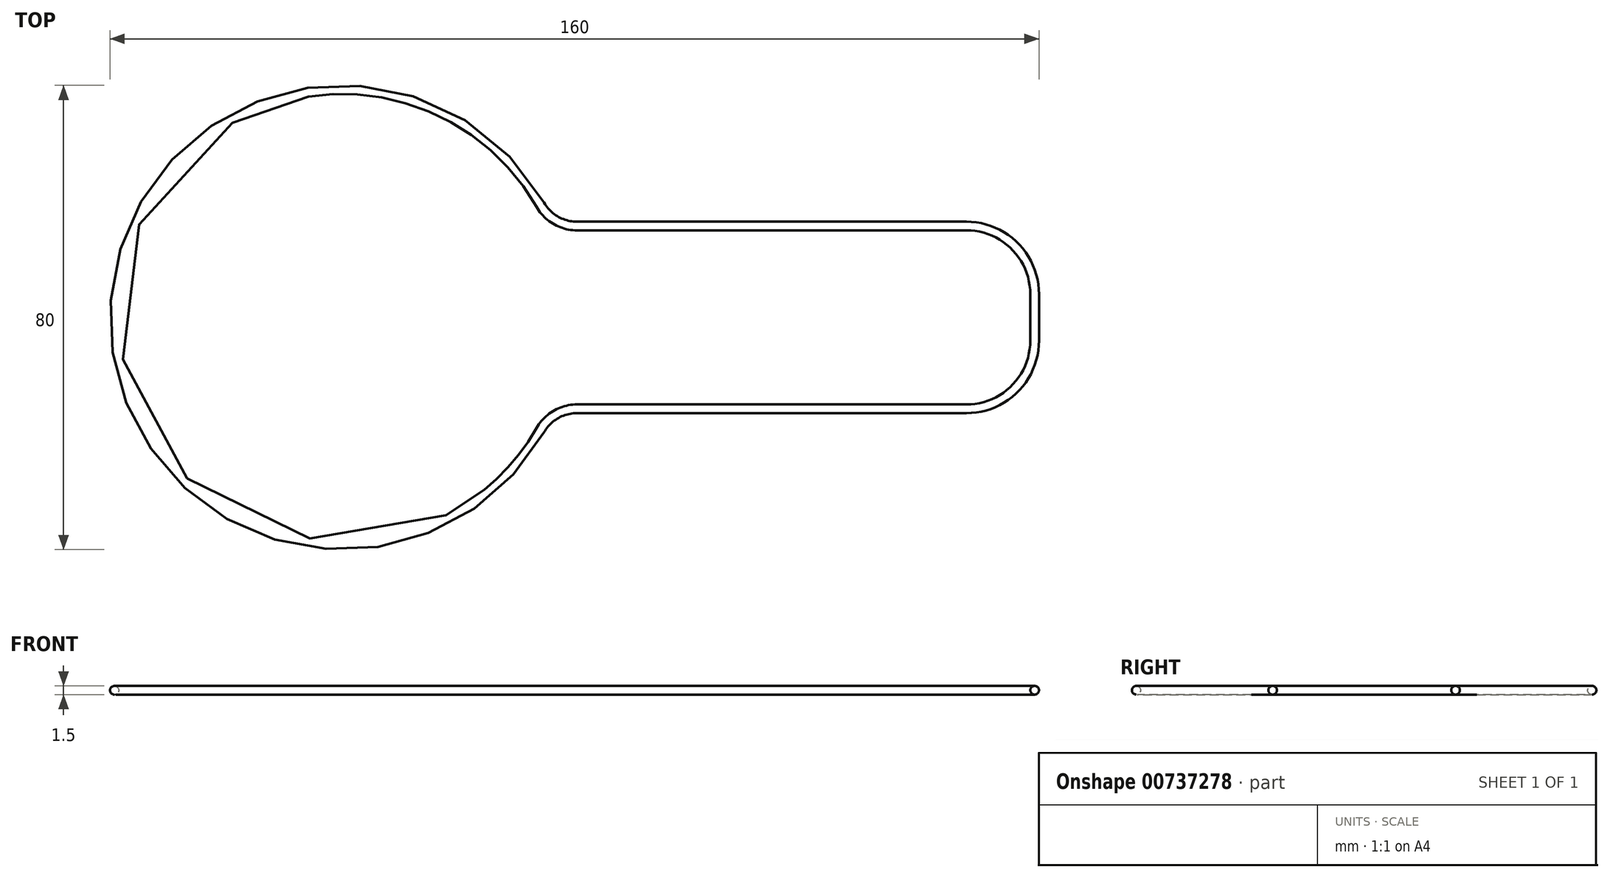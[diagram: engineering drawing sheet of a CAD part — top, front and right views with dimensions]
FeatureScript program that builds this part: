
annotation { "Feature Type Name" : "Feature", "Feature Type Description" : "" }
export const myFeature = defineFeature(function(context is Context, id is Id, definition is map)
    precondition{}
    {
        {
            var Q0;
            Q0=qCreatedBy(makeId("Top.planeOp"),FACE);
            var sketch = newSketch(context, id + "F0", { "sketchPlane" : qUnion([Q0])});
            skArc(sketch, "E0.0", {"start": v(-38.5, 0) * mm, "mid": v(-9.85, -37.22) * mm, "end": v(33.46, -19.04) * mm});
            skArc(sketch, "E1", {"start": v(40.41, -15) * mm, "mid": v(36.4, -16.08) * mm, "end": v(33.46, -19.04) * mm});
            skArc(sketch, "E2", {"start": v(107.5, -15) * mm, "mid": v(115.28, -11.78) * mm, "end": v(118.5, -4) * mm});
            skLineSegment(sketch, "E3", {"start": v(40.41, -15) * mm, "end": v(107.5, -15) * mm});
            skLineSegment(sketch, "E4", {"start": v(-52.81, 0) * mm, "end": v(142.5, 0) * mm, "construction": true});
            skLineSegment(sketch, "E5", {"start": v(118.5, -4) * mm, "end": v(118.5, 0) * mm});
            skArc(sketch, "E6.MirrorCS", {"start": v(-38.5, 0) * mm, "mid": v(-9.85, 37.22) * mm, "end": v(33.46, 19.04) * mm});
            skArc(sketch, "E7.MirrorCS", {"start": v(40.41, 15) * mm, "mid": v(36.4, 16.08) * mm, "end": v(33.46, 19.04) * mm});
            skLineSegment(sketch, "E8.MirrorCS", {"start": v(40.41, 15) * mm, "end": v(107.5, 15) * mm});
            skArc(sketch, "E9.MirrorCS", {"start": v(107.5, 15) * mm, "mid": v(115.28, 11.78) * mm, "end": v(118.5, 4) * mm});
            skLineSegment(sketch, "E10.MirrorCS", {"start": v(118.5, 4) * mm, "end": v(118.5, 0) * mm});
            skSolve(sketch);
        }
        {
            var Q0;
            Q0=qCreatedBy(makeId("Front.planeOp"),FACE);
            var sketch = newSketch(context, id + "F1", { "sketchPlane" : qUnion([Q0])});
            skLineSegment(sketch, "E11.0", {"start": v(-38.5, 0) * mm, "end": v(33.46, 0) * mm});
            skCircle(sketch, "E12", {"center": v(-39.25, 0) * mm, "radius": 0.75 * mm});
            skSolve(sketch);
        }
        {
            var Q0;
            Q0 = qSketchRegion(id + "F1", true);
            var Q1;
            Q1=sQuery(id+"F0.wireOp",EDGE,"E0.0");
            var Q2;
            Q2=sQuery(id+"F0.wireOp",EDGE,"ebaca763-9c48-4b0b-83f9-bf72b1fafb93");
            var Q3;
            Q3=sQuery(id+"F0.wireOp",EDGE,"a83afd28-553c-4998-a781-a4462ce0600c");
            var Q4;
            Q4=sQuery(id+"F0.wireOp",EDGE,"21444c6f-d51f-45d1-8dd8-12f597757086");
            var Q5;
            Q5=sQuery(id+"F0.wireOp",EDGE,"cff45251-2722-402c-a428-b0dc951107dd");
            var Q6;
            Q6=sQuery(id+"F0.wireOp",EDGE,"E2");
            var Q7;
            Q7=sQuery(id+"F0.wireOp",EDGE,"E3");
            var Q8;
            Q8=sQuery(id+"F0.wireOp",EDGE,"E1");
            var Q9;
            Q9=sQuery(id+"F0.wireOp",EDGE,"E5");
            var Q10;
            Q10=sQuery(id+"F0.wireOp",EDGE,"E6.MirrorCS");
            var Q11;
            Q11=sQuery(id+"F0.wireOp",EDGE,"E7.MirrorCS");
            var Q12;
            Q12=sQuery(id+"F0.wireOp",EDGE,"E8.MirrorCS");
            var Q13;
            Q13=sQuery(id+"F0.wireOp",EDGE,"E9.MirrorCS");
            var Q14;
            Q14=sQuery(id+"F0.wireOp",EDGE,"E10.MirrorCS");
            sweep(context, id + "F2", {"profiles" : qUnion([Q0]), "path" : qUnion([Q1, Q2, Q3, Q4, Q5, Q6, Q7, Q8, Q9, Q10, Q11, Q12, Q13, Q14])});
        }
    });
